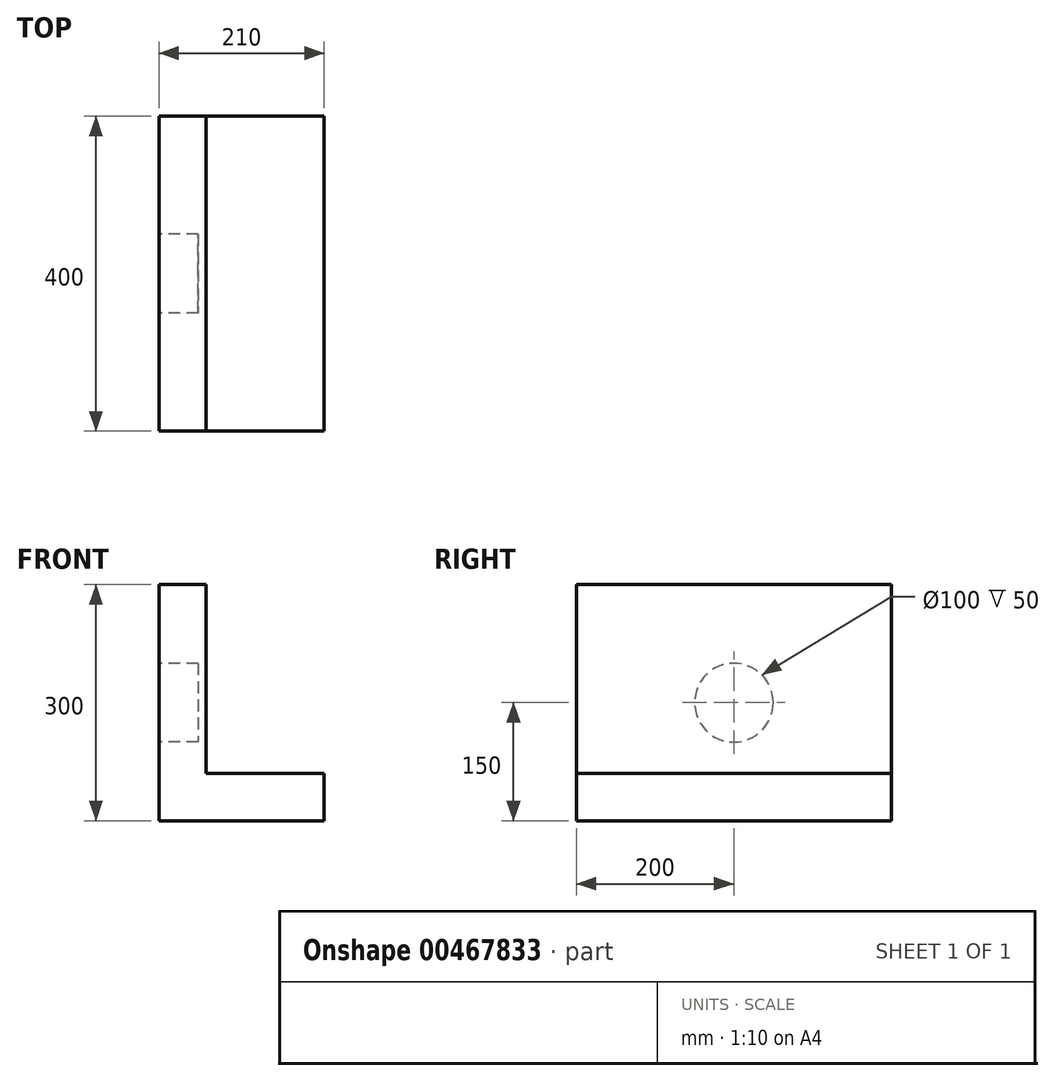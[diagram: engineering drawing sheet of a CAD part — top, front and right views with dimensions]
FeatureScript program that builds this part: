
annotation { "Feature Type Name" : "Feature", "Feature Type Description" : "" }
export const myFeature = defineFeature(function(context is Context, id is Id, definition is map)
    precondition{}
    {
        {
            var Q0;
            Q0=qCreatedBy(makeId("Front.planeOp"),FACE);
            var sketch = newSketch(context, id + "F0", { "sketchPlane" : qUnion([Q0])});
            skLineSegment(sketch, "E0.bottom", {"start": v(30, -150) * mm, "end": v(-30, -150) * mm});
            skLineSegment(sketch, "E0.top", {"start": v(30, 150) * mm, "end": v(-30, 150) * mm});
            skLineSegment(sketch, "E0.left", {"start": v(30, -90) * mm, "end": v(30, 150) * mm});
            skLineSegment(sketch, "E0.right", {"start": v(-30, -150) * mm, "end": v(-30, 150) * mm});
            skPoint(sketch, "E0.middle", {"position": v(0, 0) * mm});
            skLineSegment(sketch, "E1.bottom", {"start": v(30, -150) * mm, "end": v(180, -150) * mm});
            skLineSegment(sketch, "E1.top", {"start": v(30, -90) * mm, "end": v(180, -90) * mm});
            skLineSegment(sketch, "E1.right", {"start": v(180, -150) * mm, "end": v(180, -90) * mm});
            skSolve(sketch);
        }
        {
            var Q0;
            Q0 = qSketchRegion(id + "F0", true);
            extrude(context, id + "F1", {"entities" : qUnion([Q0]), "depth" : 400 * mm});
        }
        {
            var Q0;
            Q0=makeQuery(id+"F1.opExtrude","SWEPT_FACE",FACE,{"disambiguationData":[OSD([sQuery(id+"F0.wireOp",EDGE,"E0.right")])]});
            var sketch = newSketch(context, id + "F2", { "sketchPlane" : qUnion([Q0])});
            skCircle(sketch, "E2", {"center": v(200, 0) * mm, "radius": 50 * mm});
            skPoint(sketch, "E2.centerSnap0", {"position": v(200, 150) * mm});
            skPoint(sketch, "E2.centerSnap1", {"position": v(0, 0) * mm});
            skSolve(sketch);
        }
        {
            var Q0;
            Q0=makeQuery(id+"F2.imprint","IMPRINT",FACE,{"disambiguationData":[TD([[makeQuery(id+"F2.imprint","IMPRINT",EDGE,{"derivedFrom":sQuery(id+"F2.wireOp",EDGE,"E2")}),1.0]])]});
            extrude(context, id + "F3", {"entities" : qUnion([Q0]), "operationType" : NewBodyOperationType.REMOVE, "oppositeDirection" : true, "depth" : 50 * mm});
        }
    });
